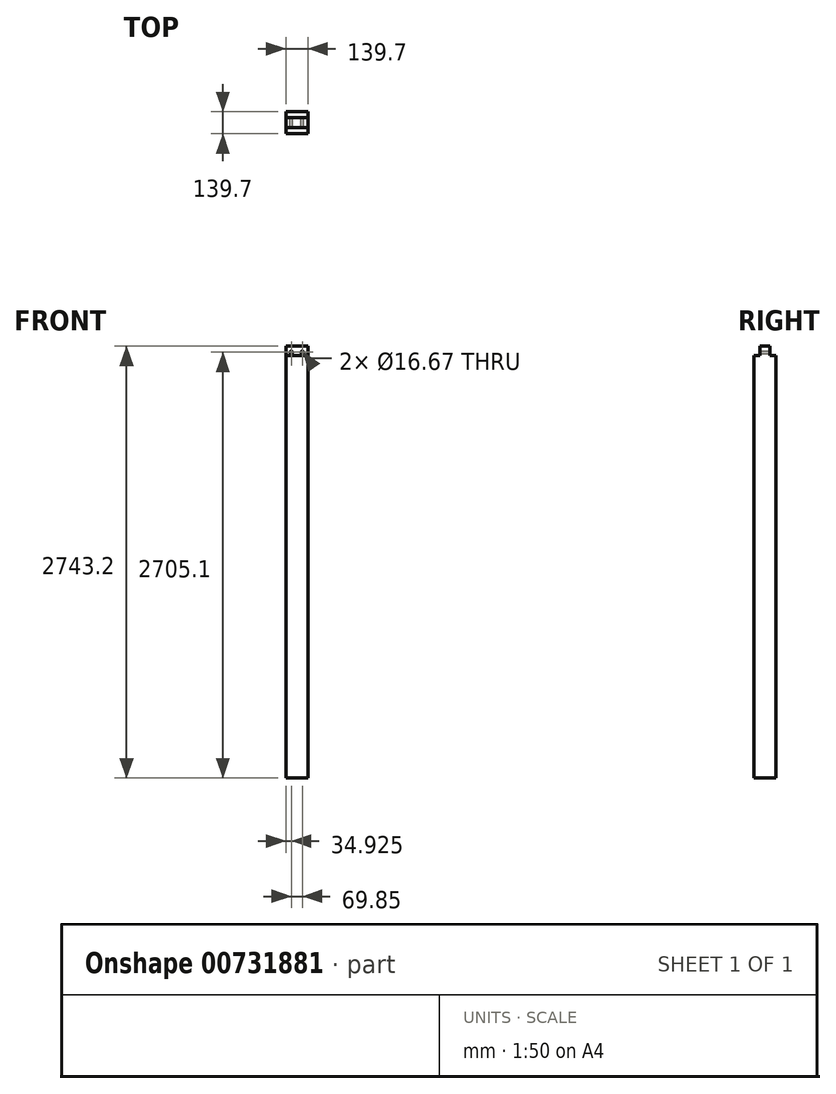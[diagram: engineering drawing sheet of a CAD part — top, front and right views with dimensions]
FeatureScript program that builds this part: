
annotation { "Feature Type Name" : "Feature", "Feature Type Description" : "" }
export const myFeature = defineFeature(function(context is Context, id is Id, definition is map)
    precondition{}
    {
        {
            var Q0;
            Q0=qCreatedBy(makeId("Top.planeOp"),FACE);
            var sketch = newSketch(context, id + "F0", { "sketchPlane" : qUnion([Q0])});
            skLineSegment(sketch, "E0.bottom", {"start": v(0, 0) * mm, "end": v(139.7, 0) * mm});
            skLineSegment(sketch, "E0.top", {"start": v(0, 139.7) * mm, "end": v(139.7, 139.7) * mm});
            skLineSegment(sketch, "E0.left", {"start": v(0, 0) * mm, "end": v(0, 139.7) * mm});
            skLineSegment(sketch, "E0.right", {"start": v(139.7, 0) * mm, "end": v(139.7, 139.7) * mm});
            skSolve(sketch);
        }
        {
            var Q0;
            Q0=makeQuery(id+"F0.imprint","IMPRINT",FACE,{"disambiguationData":[TD([[makeQuery(id+"F0.imprint","IMPRINT",EDGE,{"derivedFrom":sQuery(id+"F0.wireOp",EDGE,"E0.bottom")}),1.0]])]});
            extrude(context, id + "F1", {"entities" : qUnion([Q0]), "depth" : 2743.2 * mm, "offsetDistance" : 25.4 * mm});
        }
        {
            var Q0;
            Q0=makeQuery(id+"F1.opExtrude","SWEPT_FACE",FACE,{"disambiguationData":[OSD([sQuery(id+"F0.wireOp",EDGE,"E0.right")])]});
            var sketch = newSketch(context, id + "F2", { "sketchPlane" : qUnion([Q0])});
            skLineSegment(sketch, "E1.bottom", {"start": v(0, 2743.2) * mm, "end": v(38.1, 2743.2) * mm});
            skLineSegment(sketch, "E1.top", {"start": v(0, 2682.88) * mm, "end": v(38.1, 2682.88) * mm});
            skLineSegment(sketch, "E1.left", {"start": v(0, 2743.2) * mm, "end": v(0, 2682.88) * mm});
            skLineSegment(sketch, "E1.right", {"start": v(38.1, 2743.2) * mm, "end": v(38.1, 2682.88) * mm});
            skLineSegment(sketch, "E2.bottom", {"start": v(139.7, 2743.2) * mm, "end": v(101.6, 2743.2) * mm});
            skLineSegment(sketch, "E2.top", {"start": v(139.7, 2682.88) * mm, "end": v(101.6, 2682.88) * mm});
            skLineSegment(sketch, "E2.left", {"start": v(139.7, 2743.2) * mm, "end": v(139.7, 2682.88) * mm});
            skLineSegment(sketch, "E2.right", {"start": v(101.6, 2743.2) * mm, "end": v(101.6, 2682.88) * mm});
            skSolve(sketch);
        }
        {
            var Q0;
            Q0=makeQuery(id+"F2.imprint","IMPRINT",FACE,{"disambiguationData":[TD([[makeQuery(id+"F2.imprint","IMPRINT",EDGE,{"derivedFrom":sQuery(id+"F2.wireOp",EDGE,"E1.bottom")}),-1.0]])]});
            var Q1;
            Q1=makeQuery(id+"F2.imprint","IMPRINT",FACE,{"disambiguationData":[TD([[makeQuery(id+"F2.imprint","IMPRINT",EDGE,{"derivedFrom":sQuery(id+"F2.wireOp",EDGE,"E2.bottom")}),-1.0]])]});
            extrude(context, id + "F3", {"entities" : qUnion([Q0, Q1]), "operationType" : NewBodyOperationType.REMOVE, "endBound" : BoundingType.THROUGH_ALL, "oppositeDirection" : true, "depth" : 25.4 * mm, "offsetDistance" : 25.4 * mm});
        }
        {
            var Q0;
            Q0=makeQuery(id+"F1.opExtrude","SWEPT_FACE",FACE,{"disambiguationData":[OSD([sQuery(id+"F0.wireOp",EDGE,"E0.top")])]});
            var sketch = newSketch(context, id + "F4", { "sketchPlane" : qUnion([Q0])});
            skPoint(sketch, "E3", {"position": v(-69.85, 2682.88) * mm});
            skPoint(sketch, "E4", {"position": v(-104.78, 2705.1) * mm});
            skPoint(sketch, "E5", {"position": v(-34.93, 2705.1) * mm});
            skSolve(sketch);
        }
        {
            var Q0;
            Q0=sQuery(id+"F4.wireOp",VERTEX,"E4");
            var Q1;
            Q1=sQuery(id+"F4.wireOp",VERTEX,"E5");
            var Q2;
            Q2=makeQuery(id+"F1.opExtrude","SWEPT_BODY",BODY,{"disambiguationData":[OSD([sQuery(id+"F0.wireOp",EDGE,"E0.bottom"),sQuery(id+"F0.wireOp",EDGE,"E0.top"),sQuery(id+"F0.wireOp",EDGE,"E0.left"),sQuery(id+"F0.wireOp",EDGE,"E0.right")])]});
            hole(context, id + "F5", {"style" : HoleStyle.SIMPLE, "endStyle" : HoleEndStyle.THROUGH, "standardTappedOrClearance" : lookupTablePath({ "fit" : "Normal (ASME)", "standard" : "ANSI", "size" : "5/8", "type" : "Clearance" }), "standardBlindInLast" : lookupTablePath({ "fit" : "Free", "standard" : "ANSI", "size" : "5/8", "type" : "Clearance" }), "holeDiameter" : 16.67 * mm, "majorDiameter" : 6.35 * mm, "isTappedThrough" : true, "tappedDepth" : 12.7 * mm, "tapClearance" : 3, "startFromSketch" : true, "locations" : qUnion([Q0, Q1]), "scope" : qUnion([Q2])});
        }
    });
